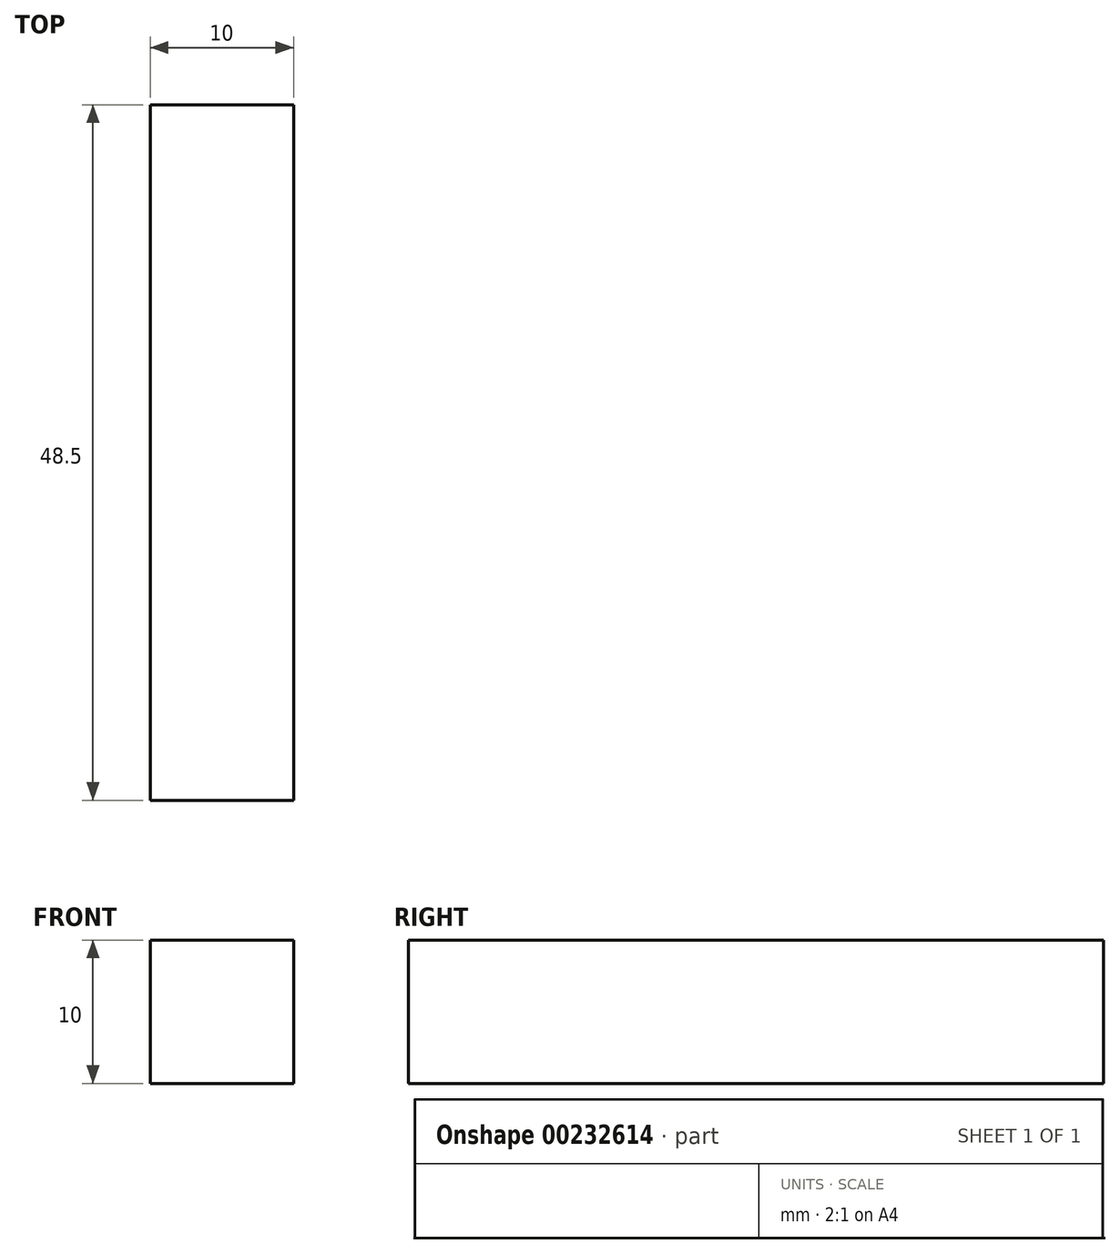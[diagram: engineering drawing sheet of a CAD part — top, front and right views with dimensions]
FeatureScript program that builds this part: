
annotation { "Feature Type Name" : "Feature", "Feature Type Description" : "" }
export const myFeature = defineFeature(function(context is Context, id is Id, definition is map)
    precondition{}
    {
        {
            var Q0;
            Q0=qCreatedBy(makeId("Top.planeOp"),FACE);
            var sketch = newSketch(context, id + "F0", { "sketchPlane" : qUnion([Q0])});
            skLineSegment(sketch, "E0.bottom", {"start": v(0, 0) * mm, "end": v(10, 0) * mm});
            skLineSegment(sketch, "E0.top", {"start": v(0, 48.5) * mm, "end": v(10, 48.5) * mm});
            skLineSegment(sketch, "E0.left", {"start": v(0, 0) * mm, "end": v(0, 48.5) * mm});
            skLineSegment(sketch, "E0.right", {"start": v(10, 0) * mm, "end": v(10, 48.5) * mm});
            skSolve(sketch);
        }
        {
            var Q0;
            Q0 = qSketchRegion(id + "F0", true);
            extrude(context, id + "F1", {"entities" : qUnion([Q0]), "depth" : 10 * mm});
        }
    });
